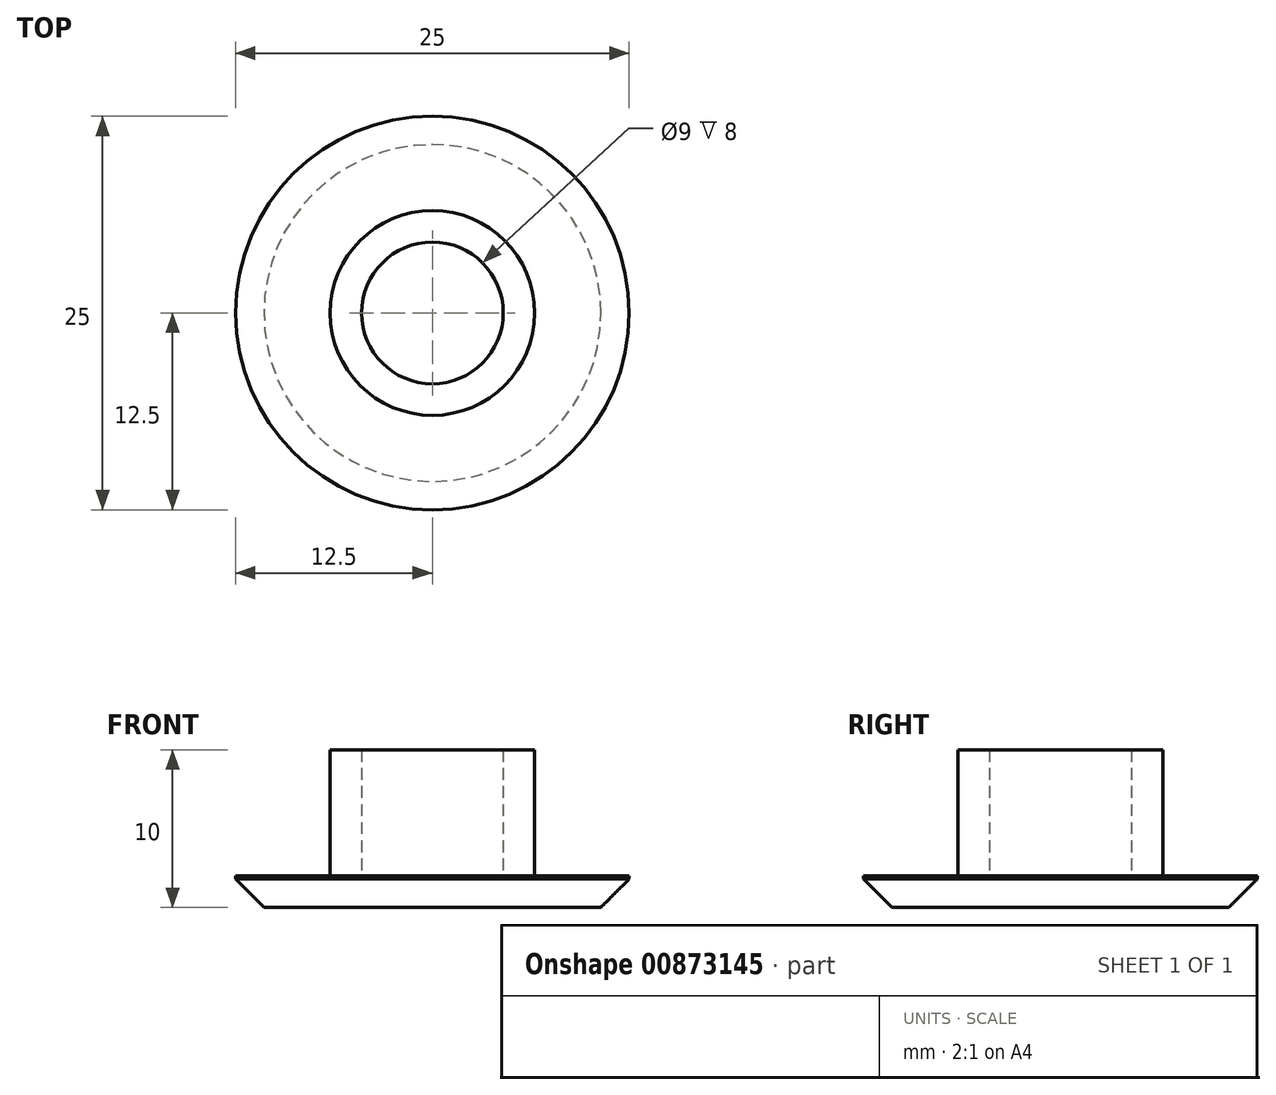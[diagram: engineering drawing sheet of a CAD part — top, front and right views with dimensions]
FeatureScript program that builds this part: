
annotation { "Feature Type Name" : "Feature", "Feature Type Description" : "" }
export const myFeature = defineFeature(function(context is Context, id is Id, definition is map)
    precondition{}
    {
        {
            var Q0;
            Q0=qCreatedBy(makeId("Top.planeOp"),FACE);
            var sketch = newSketch(context, id + "F0", { "sketchPlane" : qUnion([Q0])});
            skCircle(sketch, "E0", {"center": v(0, 0) * mm, "radius": 4.5 * mm});
            skCircle(sketch, "E1.0", {"center": v(0, 0) * mm, "radius": 6.5 * mm});
            skCircle(sketch, "E2", {"center": v(0, 0) * mm, "radius": 12.5 * mm});
            skSolve(sketch);
        }
        {
            var Q0;
            Q0=makeQuery(id+"F0.imprint","IMPRINT",FACE,{"disambiguationData":[TD([[makeQuery(id+"F0.imprint","IMPRINT",EDGE,{"derivedFrom":sQuery(id+"F0.wireOp",EDGE,"E1.0")}),-1.0]])]});
            var Q1;
            Q1=makeQuery(id+"F0.imprint","IMPRINT",FACE,{"disambiguationData":[TD([[makeQuery(id+"F0.imprint","IMPRINT",EDGE,{"derivedFrom":sQuery(id+"F0.wireOp",EDGE,"E0")}),-1.0]])]});
            var Q2;
            Q2=makeQuery(id+"F0.imprint","IMPRINT",FACE,{"disambiguationData":[TD([[makeQuery(id+"F0.imprint","IMPRINT",EDGE,{"derivedFrom":sQuery(id+"F0.wireOp",EDGE,"E0")}),1.0]])]});
            extrude(context, id + "F1", {"entities" : qUnion([Q0, Q1, Q2]), "depth" : 2 * mm, "offsetDistance" : 25 * mm});
        }
        {
            var Q0;
            Q0=makeQuery(id+"F0.imprint","IMPRINT",FACE,{"disambiguationData":[TD([[makeQuery(id+"F0.imprint","IMPRINT",EDGE,{"derivedFrom":sQuery(id+"F0.wireOp",EDGE,"E0")}),-1.0]])]});
            extrude(context, id + "F2", {"entities" : qUnion([Q0]), "operationType" : NewBodyOperationType.ADD, "depth" : 10 * mm, "offsetDistance" : 25 * mm});
        }
        {
            var Q0;
            Q0=makeQuery(id+"F1.opExtrude","CAP_EDGE",EDGE,{"disambiguationData":[OSD([sQuery(id+"F0.wireOp",EDGE,"E2")])],"isStart":true});
            chamfer(context, id + "F3", {"entities" : qUnion([Q0]), "width" : 1.8 * mm, "tangentPropagation" : true});
        }
    });
